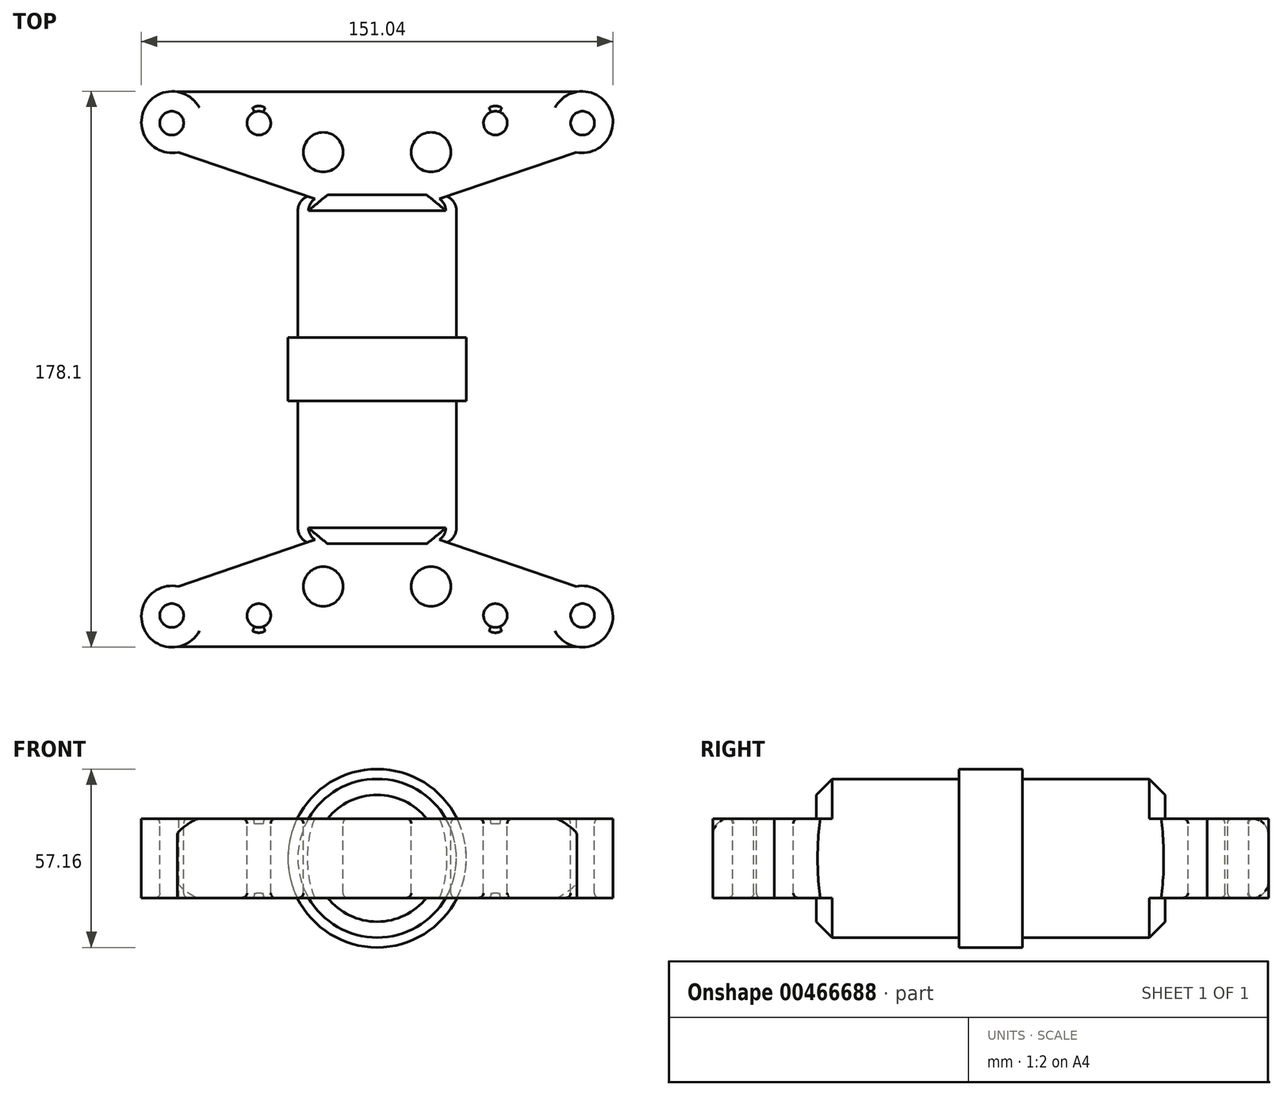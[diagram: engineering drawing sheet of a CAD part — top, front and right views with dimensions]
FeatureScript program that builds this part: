
annotation { "Feature Type Name" : "Feature", "Feature Type Description" : "" }
export const myFeature = defineFeature(function(context is Context, id is Id, definition is map)
    precondition{}
    {
        {
            var Q0;
            Q0=qCreatedBy(makeId("Top.planeOp"),FACE);
            var sketch = newSketch(context, id + "F0", { "sketchPlane" : qUnion([Q0])});
            skLineSegment(sketch, "E0.bottom", {"start": v(0, 0) * mm, "end": v(-76.2, 0) * mm, "construction": true});
            skLineSegment(sketch, "E0.left", {"start": v(0, 0) * mm, "end": v(0, 88.9) * mm, "construction": true});
            skLineSegment(sketch, "E0.right", {"start": v(-76.2, 0) * mm, "end": v(-76.2, 88.9) * mm, "construction": true});
            skLineSegment(sketch, "E1.MirrorCS", {"start": v(0, 88.9) * mm, "end": v(76.2, 88.9) * mm, "construction": true});
            skLineSegment(sketch, "E2.MirrorCS", {"start": v(76.2, 0) * mm, "end": v(76.2, 88.9) * mm, "construction": true});
            skLineSegment(sketch, "E3.MirrorCS", {"start": v(0, 0) * mm, "end": v(76.2, 0) * mm});
            skLineSegment(sketch, "E4.MirrorCS", {"start": v(0, 0) * mm, "end": v(0, -88.9) * mm, "construction": true});
            skLineSegment(sketch, "E5.MirrorCS", {"start": v(-76.2, 0) * mm, "end": v(-76.2, -88.9) * mm, "construction": true});
            skLineSegment(sketch, "E6.MirrorCS", {"start": v(0, 0) * mm, "end": v(76.2, 0) * mm, "construction": true});
            skLineSegment(sketch, "E7.MirrorCS", {"start": v(76.2, 0) * mm, "end": v(76.2, -88.9) * mm, "construction": true});
            skLineSegment(sketch, "E8.MirrorCS", {"start": v(0, -88.9) * mm, "end": v(76.2, -88.9) * mm, "construction": true});
            skArc(sketch, "E9", {"start": v(-63.96, 88.9) * mm, "mid": v(-75.52, 79.06) * mm, "end": v(-63.7, 69.55) * mm});
            skLineSegment(sketch, "E10", {"start": v(-63.96, 88.9) * mm, "end": v(0, 88.9) * mm});
            skLineSegment(sketch, "E11", {"start": v(-63.7, 69.55) * mm, "end": v(-20.52, 54.8) * mm});
            skLineSegment(sketch, "E12", {"start": v(-20.52, 54.8) * mm, "end": v(-20.52, 0) * mm});
            skLineSegment(sketch, "E13.MirrorCS", {"start": v(20.52, 54.8) * mm, "end": v(20.52, 0) * mm});
            skLineSegment(sketch, "E14.MirrorCS", {"start": v(63.7, 69.55) * mm, "end": v(20.52, 54.8) * mm});
            skLineSegment(sketch, "E15.MirrorCS", {"start": v(63.96, 88.9) * mm, "end": v(0, 88.9) * mm});
            skArc(sketch, "E16.MirrorCS", {"start": v(63.96, 88.9) * mm, "mid": v(75.52, 79.06) * mm, "end": v(63.7, 69.55) * mm});
            skLineSegment(sketch, "E17.MirrorCS", {"start": v(-63.96, -88.9) * mm, "end": v(0, -88.9) * mm});
            skArc(sketch, "E18.MirrorCS", {"start": v(-63.96, -88.9) * mm, "mid": v(-75.52, -79.06) * mm, "end": v(-63.7, -69.55) * mm});
            skLineSegment(sketch, "E19.MirrorCS", {"start": v(-20.52, -54.8) * mm, "end": v(-20.52, 0) * mm});
            skLineSegment(sketch, "E20.MirrorCS", {"start": v(-63.7, -69.55) * mm, "end": v(-20.52, -54.8) * mm});
            skLineSegment(sketch, "E21.MirrorCS", {"start": v(20.52, -54.8) * mm, "end": v(20.52, 0) * mm});
            skLineSegment(sketch, "E22.MirrorCS", {"start": v(63.7, -69.55) * mm, "end": v(20.52, -54.8) * mm});
            skArc(sketch, "E23.MirrorCS", {"start": v(63.96, -88.9) * mm, "mid": v(75.52, -79.06) * mm, "end": v(63.7, -69.55) * mm});
            skLineSegment(sketch, "E24.MirrorCS", {"start": v(63.96, -88.9) * mm, "end": v(0, -88.9) * mm});
            skSolve(sketch);
        }
        {
            var Q0;
            Q0=qCreatedBy(makeId("Front.planeOp"),FACE);
            var sketch = newSketch(context, id + "F1", { "sketchPlane" : qUnion([Q0])});
            skCircle(sketch, "E25", {"center": v(0, 0) * mm, "radius": 25.4 * mm});
            skSolve(sketch);
        }
        {
            var Q0;
            Q0 = qSketchRegion(id + "F0", true);
            extrude(context, id + "F2", {"entities" : qUnion([Q0]), "depth" : 12.7 * mm, "hasSecondDirection" : true, "secondDirectionOppositeDirection" : true, "secondDirectionDepth" : 12.7 * mm});
        }
        {
            var Q0;
            Q0 = qSketchRegion(id + "F1", true);
            extrude(context, id + "F3", {"entities" : qUnion([Q0]), "operationType" : NewBodyOperationType.ADD, "depth" : 55.88 * mm, "hasSecondDirection" : true, "secondDirectionOppositeDirection" : true, "secondDirectionDepth" : 55.88 * mm});
        }
        {
            var Q0;
            {var subQ0=sQuery(id+"F1.wireOp",EDGE,"E25");Q0=makeQuery(id+"F3.boolean.opBoolean","SPLIT",EDGE,{"disambiguationData":[TD([makeQuery(id+"F2.opExtrude","CAP_FACE",FACE,{"disambiguationData":[OSD([sQuery(id+"F0.wireOp",EDGE,"E9"),sQuery(id+"F0.wireOp",EDGE,"E10"),sQuery(id+"F0.wireOp",EDGE,"E11"),sQuery(id+"F0.wireOp",EDGE,"E12"),sQuery(id+"F0.wireOp",EDGE,"E14.MirrorCS"),sQuery(id+"F0.wireOp",EDGE,"E15.MirrorCS"),sQuery(id+"F0.wireOp",EDGE,"E16.MirrorCS"),sQuery(id+"F0.wireOp",EDGE,"E13.MirrorCS"),sQuery(id+"F0.wireOp",EDGE,"E17.MirrorCS"),sQuery(id+"F0.wireOp",EDGE,"E18.MirrorCS"),sQuery(id+"F0.wireOp",EDGE,"E19.MirrorCS"),sQuery(id+"F0.wireOp",EDGE,"E20.MirrorCS"),sQuery(id+"F0.wireOp",EDGE,"E21.MirrorCS"),sQuery(id+"F0.wireOp",EDGE,"E22.MirrorCS"),sQuery(id+"F0.wireOp",EDGE,"E23.MirrorCS"),sQuery(id+"F0.wireOp",EDGE,"E24.MirrorCS")])],"isStart":false})])],"derivedFrom":makeQuery(id+"F3.opExtrude","CAP_EDGE",EDGE,{"disambiguationData":[OSD([subQ0])],"isStart":true})});}
            var Q1;
            {var subQ0=sQuery(id+"F1.wireOp",EDGE,"E25");Q1=makeQuery(id+"F3.boolean.opBoolean","SPLIT",EDGE,{"disambiguationData":[TD([makeQuery(id+"F2.opExtrude","CAP_FACE",FACE,{"disambiguationData":[OSD([sQuery(id+"F0.wireOp",EDGE,"E9"),sQuery(id+"F0.wireOp",EDGE,"E10"),sQuery(id+"F0.wireOp",EDGE,"E11"),sQuery(id+"F0.wireOp",EDGE,"E12"),sQuery(id+"F0.wireOp",EDGE,"E14.MirrorCS"),sQuery(id+"F0.wireOp",EDGE,"E15.MirrorCS"),sQuery(id+"F0.wireOp",EDGE,"E16.MirrorCS"),sQuery(id+"F0.wireOp",EDGE,"E13.MirrorCS"),sQuery(id+"F0.wireOp",EDGE,"E17.MirrorCS"),sQuery(id+"F0.wireOp",EDGE,"E18.MirrorCS"),sQuery(id+"F0.wireOp",EDGE,"E19.MirrorCS"),sQuery(id+"F0.wireOp",EDGE,"E20.MirrorCS"),sQuery(id+"F0.wireOp",EDGE,"E21.MirrorCS"),sQuery(id+"F0.wireOp",EDGE,"E22.MirrorCS"),sQuery(id+"F0.wireOp",EDGE,"E23.MirrorCS"),sQuery(id+"F0.wireOp",EDGE,"E24.MirrorCS")])],"isStart":true})])],"derivedFrom":makeQuery(id+"F3.opExtrude","CAP_EDGE",EDGE,{"disambiguationData":[OSD([subQ0])],"isStart":true})});}
            var Q2;
            {var subQ0=sQuery(id+"F1.wireOp",EDGE,"E25");Q2=makeQuery(id+"F3.boolean.opBoolean","SPLIT",EDGE,{"disambiguationData":[TD([makeQuery(id+"F2.opExtrude","CAP_FACE",FACE,{"disambiguationData":[OSD([sQuery(id+"F0.wireOp",EDGE,"E9"),sQuery(id+"F0.wireOp",EDGE,"E10"),sQuery(id+"F0.wireOp",EDGE,"E11"),sQuery(id+"F0.wireOp",EDGE,"E12"),sQuery(id+"F0.wireOp",EDGE,"E14.MirrorCS"),sQuery(id+"F0.wireOp",EDGE,"E15.MirrorCS"),sQuery(id+"F0.wireOp",EDGE,"E16.MirrorCS"),sQuery(id+"F0.wireOp",EDGE,"E13.MirrorCS"),sQuery(id+"F0.wireOp",EDGE,"E17.MirrorCS"),sQuery(id+"F0.wireOp",EDGE,"E18.MirrorCS"),sQuery(id+"F0.wireOp",EDGE,"E19.MirrorCS"),sQuery(id+"F0.wireOp",EDGE,"E20.MirrorCS"),sQuery(id+"F0.wireOp",EDGE,"E21.MirrorCS"),sQuery(id+"F0.wireOp",EDGE,"E22.MirrorCS"),sQuery(id+"F0.wireOp",EDGE,"E23.MirrorCS"),sQuery(id+"F0.wireOp",EDGE,"E24.MirrorCS")])],"isStart":true})])],"derivedFrom":makeQuery(id+"F3.opExtrude","CAP_EDGE",EDGE,{"disambiguationData":[OSD([subQ0])],"isStart":false})});}
            var Q3;
            {var subQ0=sQuery(id+"F1.wireOp",EDGE,"E25");Q3=makeQuery(id+"F3.boolean.opBoolean","SPLIT",EDGE,{"disambiguationData":[TD([makeQuery(id+"F2.opExtrude","CAP_FACE",FACE,{"disambiguationData":[OSD([sQuery(id+"F0.wireOp",EDGE,"E9"),sQuery(id+"F0.wireOp",EDGE,"E10"),sQuery(id+"F0.wireOp",EDGE,"E11"),sQuery(id+"F0.wireOp",EDGE,"E12"),sQuery(id+"F0.wireOp",EDGE,"E14.MirrorCS"),sQuery(id+"F0.wireOp",EDGE,"E15.MirrorCS"),sQuery(id+"F0.wireOp",EDGE,"E16.MirrorCS"),sQuery(id+"F0.wireOp",EDGE,"E13.MirrorCS"),sQuery(id+"F0.wireOp",EDGE,"E17.MirrorCS"),sQuery(id+"F0.wireOp",EDGE,"E18.MirrorCS"),sQuery(id+"F0.wireOp",EDGE,"E19.MirrorCS"),sQuery(id+"F0.wireOp",EDGE,"E20.MirrorCS"),sQuery(id+"F0.wireOp",EDGE,"E21.MirrorCS"),sQuery(id+"F0.wireOp",EDGE,"E22.MirrorCS"),sQuery(id+"F0.wireOp",EDGE,"E23.MirrorCS"),sQuery(id+"F0.wireOp",EDGE,"E24.MirrorCS")])],"isStart":false})])],"derivedFrom":makeQuery(id+"F3.opExtrude","CAP_EDGE",EDGE,{"disambiguationData":[OSD([subQ0])],"isStart":false})});}
            chamfer(context, id + "F4", {"entities" : qUnion([Q0, Q1, Q2, Q3]), "width" : 5.08 * mm, "tangentPropagation" : true});
        }
        {
            var Q0;
            {var subQ0=sQuery(id+"F1.wireOp",EDGE,"E25");Q0=makeQuery(id+"F3.boolean.opBoolean","SPLIT",EDGE,{"disambiguationData":[TD([makeQuery(id+"F2.opExtrude","SWEPT_FACE",FACE,{"disambiguationData":[OSD([sQuery(id+"F0.wireOp",EDGE,"E14.MirrorCS")])]})])],"derivedFrom":makeQuery(id+"F3.opExtrude","CAP_EDGE",EDGE,{"disambiguationData":[OSD([subQ0])],"isStart":true})});}
            var Q1;
            {var subQ0=sQuery(id+"F1.wireOp",EDGE,"E25");Q1=makeQuery(id+"F3.boolean.opBoolean","SPLIT",EDGE,{"disambiguationData":[TD([makeQuery(id+"F2.opExtrude","SWEPT_FACE",FACE,{"disambiguationData":[OSD([sQuery(id+"F0.wireOp",EDGE,"E11")])]})])],"derivedFrom":makeQuery(id+"F3.opExtrude","CAP_EDGE",EDGE,{"disambiguationData":[OSD([subQ0])],"isStart":true})});}
            var Q2;
            {var subQ0=sQuery(id+"F1.wireOp",EDGE,"E25");Q2=makeQuery(id+"F3.boolean.opBoolean","SPLIT",EDGE,{"disambiguationData":[TD([makeQuery(id+"F2.opExtrude","SWEPT_FACE",FACE,{"disambiguationData":[OSD([sQuery(id+"F0.wireOp",EDGE,"E20.MirrorCS")])]})])],"derivedFrom":makeQuery(id+"F3.opExtrude","CAP_EDGE",EDGE,{"disambiguationData":[OSD([subQ0])],"isStart":false})});}
            var Q3;
            {var subQ0=sQuery(id+"F1.wireOp",EDGE,"E25");Q3=makeQuery(id+"F3.boolean.opBoolean","SPLIT",EDGE,{"disambiguationData":[TD([makeQuery(id+"F2.opExtrude","SWEPT_FACE",FACE,{"disambiguationData":[OSD([sQuery(id+"F0.wireOp",EDGE,"E22.MirrorCS")])]})])],"derivedFrom":makeQuery(id+"F3.opExtrude","CAP_EDGE",EDGE,{"disambiguationData":[OSD([subQ0])],"isStart":false})});}
            fillet(context, id + "F5", {"entities" : qUnion([Q0, Q1, Q2, Q3]), "radius" : 5.08 * mm, "tangentPropagation" : true, "allowEdgeOverflow" : false});
        }
        {
            var Q0;
            Q0=makeQuery(id+"F2.opExtrude","CAP_EDGE",EDGE,{"disambiguationData":[OSD([sQuery(id+"F0.wireOp",EDGE,"E17.MirrorCS"),sQuery(id+"F0.wireOp",EDGE,"E24.MirrorCS")])],"isStart":false});
            var Q1;
            Q1=makeQuery(id+"F2.opExtrude","CAP_EDGE",EDGE,{"disambiguationData":[OSD([sQuery(id+"F0.wireOp",EDGE,"E10"),sQuery(id+"F0.wireOp",EDGE,"E15.MirrorCS")])],"isStart":false});
            var Q2;
            Q2=makeQuery(id+"F2.opExtrude","CAP_EDGE",EDGE,{"disambiguationData":[OSD([sQuery(id+"F0.wireOp",EDGE,"E10"),sQuery(id+"F0.wireOp",EDGE,"E15.MirrorCS")])],"isStart":true});
            fillet(context, id + "F6", {"entities" : qUnion([Q0, Q1, Q2]), "radius" : 5.08 * mm, "tangentPropagation" : true, "allowEdgeOverflow" : false});
        }
        {
            var Q0;
            Q0=qCreatedBy(makeId("Top.planeOp"),FACE);
            var sketch = newSketch(context, id + "F7", { "sketchPlane" : qUnion([Q0])});
            skLineSegment(sketch, "E26", {"start": v(-65.8, 78.88) * mm, "end": v(0, 78.88) * mm, "construction": true});
            skCircle(sketch, "E27", {"center": v(-65.8, 78.88) * mm, "radius": 3.81 * mm});
            skCircle(sketch, "E28", {"center": v(-37.89, 78.88) * mm, "radius": 3.81 * mm});
            skLineSegment(sketch, "E29", {"start": v(-17.28, 78.88) * mm, "end": v(-17.28, 69.57) * mm, "construction": true});
            skLineSegment(sketch, "E30", {"start": v(-17.28, 69.57) * mm, "end": v(0, 69.57) * mm, "construction": true});
            skCircle(sketch, "E31", {"center": v(-17.28, 69.57) * mm, "radius": 6.35 * mm});
            skCircle(sketch, "E32.MirrorC", {"center": v(17.28, 69.57) * mm, "radius": 6.35 * mm});
            skCircle(sketch, "E33.MirrorC", {"center": v(37.89, 78.88) * mm, "radius": 3.81 * mm});
            skCircle(sketch, "E34.MirrorC", {"center": v(65.8, 78.88) * mm, "radius": 3.81 * mm});
            skCircle(sketch, "E35.MirrorC", {"center": v(65.8, -78.88) * mm, "radius": 3.81 * mm});
            skCircle(sketch, "E36.MirrorC", {"center": v(37.89, -78.88) * mm, "radius": 3.81 * mm});
            skCircle(sketch, "E37.MirrorC", {"center": v(17.28, -69.57) * mm, "radius": 6.35 * mm});
            skCircle(sketch, "E38.MirrorC", {"center": v(-17.28, -69.57) * mm, "radius": 6.35 * mm});
            skCircle(sketch, "E39.MirrorC", {"center": v(-37.89, -78.88) * mm, "radius": 3.81 * mm});
            skCircle(sketch, "E40.MirrorC", {"center": v(-65.8, -78.88) * mm, "radius": 3.81 * mm});
            skSolve(sketch);
        }
        {
            var Q0;
            Q0 = qSketchRegion(id + "F7", true);
            extrude(context, id + "F8", {"entities" : qUnion([Q0]), "operationType" : NewBodyOperationType.REMOVE, "oppositeDirection" : true, "depth" : 25.4 * mm, "hasSecondDirection" : true, "secondDirectionOppositeDirection" : false, "secondDirectionDepth" : 25.4 * mm});
        }
        {
            var Q0;
            {var subQ0=sQuery(id+"F0.wireOp",EDGE,"E14.MirrorCS");var subQ1=sQuery(id+"F0.wireOp",EDGE,"E11");var subQ3=sQuery(id+"F0.wireOp",EDGE,"E15.MirrorCS");var subQ4=sQuery(id+"F0.wireOp",EDGE,"E10");var subQ5=sQuery(id+"F0.wireOp",EDGE,"E9");var subQ6=sQuery(id+"F0.wireOp",EDGE,"E16.MirrorCS");Q0=makeQuery(id+"F8.boolean.opBoolean","INTERSECT",EDGE,{"derivedFrom":[makeQuery(id+"F3.boolean.opBoolean","SPLIT",FACE,{"disambiguationData":[TD([makeQuery(id+"F2.opExtrude","SWEPT_FACE",FACE,{"disambiguationData":[OSD([subQ5])]})])],"derivedFrom":makeQuery(id+"F2.opExtrude","CAP_FACE",FACE,{"disambiguationData":[OSD([subQ5,subQ4,subQ1,sQuery(id+"F0.wireOp",EDGE,"E12"),subQ0,subQ3,subQ6,sQuery(id+"F0.wireOp",EDGE,"E13.MirrorCS"),sQuery(id+"F0.wireOp",EDGE,"E17.MirrorCS"),sQuery(id+"F0.wireOp",EDGE,"E18.MirrorCS"),sQuery(id+"F0.wireOp",EDGE,"E19.MirrorCS"),sQuery(id+"F0.wireOp",EDGE,"E20.MirrorCS"),sQuery(id+"F0.wireOp",EDGE,"E21.MirrorCS"),sQuery(id+"F0.wireOp",EDGE,"E22.MirrorCS"),sQuery(id+"F0.wireOp",EDGE,"E23.MirrorCS"),sQuery(id+"F0.wireOp",EDGE,"E24.MirrorCS")])],"isStart":false})}),makeQuery(id+"F8.opExtrude","SWEPT_FACE",FACE,{"disambiguationData":[OSD([sQuery(id+"F7.wireOp",EDGE,"E27")])]})]});}
            var Q1;
            {var subQ0=sQuery(id+"F0.wireOp",EDGE,"E14.MirrorCS");var subQ1=sQuery(id+"F0.wireOp",EDGE,"E11");var subQ3=sQuery(id+"F0.wireOp",EDGE,"E15.MirrorCS");var subQ4=sQuery(id+"F0.wireOp",EDGE,"E10");var subQ5=sQuery(id+"F0.wireOp",EDGE,"E9");var subQ6=sQuery(id+"F0.wireOp",EDGE,"E16.MirrorCS");Q1=makeQuery(id+"F8.boolean.opBoolean","INTERSECT",EDGE,{"derivedFrom":[makeQuery(id+"F3.boolean.opBoolean","SPLIT",FACE,{"disambiguationData":[TD([makeQuery(id+"F2.opExtrude","SWEPT_FACE",FACE,{"disambiguationData":[OSD([subQ5])]})])],"derivedFrom":makeQuery(id+"F2.opExtrude","CAP_FACE",FACE,{"disambiguationData":[OSD([subQ5,subQ4,subQ1,sQuery(id+"F0.wireOp",EDGE,"E12"),subQ0,subQ3,subQ6,sQuery(id+"F0.wireOp",EDGE,"E13.MirrorCS"),sQuery(id+"F0.wireOp",EDGE,"E17.MirrorCS"),sQuery(id+"F0.wireOp",EDGE,"E18.MirrorCS"),sQuery(id+"F0.wireOp",EDGE,"E19.MirrorCS"),sQuery(id+"F0.wireOp",EDGE,"E20.MirrorCS"),sQuery(id+"F0.wireOp",EDGE,"E21.MirrorCS"),sQuery(id+"F0.wireOp",EDGE,"E22.MirrorCS"),sQuery(id+"F0.wireOp",EDGE,"E23.MirrorCS"),sQuery(id+"F0.wireOp",EDGE,"E24.MirrorCS")])],"isStart":false})}),makeQuery(id+"F8.opExtrude","SWEPT_FACE",FACE,{"disambiguationData":[OSD([sQuery(id+"F7.wireOp",EDGE,"E28")])]})]});}
            var Q2;
            {var subQ0=sQuery(id+"F0.wireOp",EDGE,"E14.MirrorCS");var subQ1=sQuery(id+"F0.wireOp",EDGE,"E11");var subQ3=sQuery(id+"F0.wireOp",EDGE,"E15.MirrorCS");var subQ4=sQuery(id+"F0.wireOp",EDGE,"E10");var subQ5=sQuery(id+"F0.wireOp",EDGE,"E9");var subQ6=sQuery(id+"F0.wireOp",EDGE,"E16.MirrorCS");Q2=makeQuery(id+"F8.boolean.opBoolean","INTERSECT",EDGE,{"derivedFrom":[makeQuery(id+"F3.boolean.opBoolean","SPLIT",FACE,{"disambiguationData":[TD([makeQuery(id+"F2.opExtrude","SWEPT_FACE",FACE,{"disambiguationData":[OSD([subQ5])]})])],"derivedFrom":makeQuery(id+"F2.opExtrude","CAP_FACE",FACE,{"disambiguationData":[OSD([subQ5,subQ4,subQ1,sQuery(id+"F0.wireOp",EDGE,"E12"),subQ0,subQ3,subQ6,sQuery(id+"F0.wireOp",EDGE,"E13.MirrorCS"),sQuery(id+"F0.wireOp",EDGE,"E17.MirrorCS"),sQuery(id+"F0.wireOp",EDGE,"E18.MirrorCS"),sQuery(id+"F0.wireOp",EDGE,"E19.MirrorCS"),sQuery(id+"F0.wireOp",EDGE,"E20.MirrorCS"),sQuery(id+"F0.wireOp",EDGE,"E21.MirrorCS"),sQuery(id+"F0.wireOp",EDGE,"E22.MirrorCS"),sQuery(id+"F0.wireOp",EDGE,"E23.MirrorCS"),sQuery(id+"F0.wireOp",EDGE,"E24.MirrorCS")])],"isStart":false})}),makeQuery(id+"F8.opExtrude","SWEPT_FACE",FACE,{"disambiguationData":[OSD([sQuery(id+"F7.wireOp",EDGE,"E31")])]})]});}
            var Q3;
            {var subQ0=sQuery(id+"F0.wireOp",EDGE,"E14.MirrorCS");var subQ1=sQuery(id+"F0.wireOp",EDGE,"E11");var subQ3=sQuery(id+"F0.wireOp",EDGE,"E15.MirrorCS");var subQ4=sQuery(id+"F0.wireOp",EDGE,"E10");var subQ5=sQuery(id+"F0.wireOp",EDGE,"E9");var subQ6=sQuery(id+"F0.wireOp",EDGE,"E16.MirrorCS");Q3=makeQuery(id+"F8.boolean.opBoolean","INTERSECT",EDGE,{"derivedFrom":[makeQuery(id+"F3.boolean.opBoolean","SPLIT",FACE,{"disambiguationData":[TD([makeQuery(id+"F2.opExtrude","SWEPT_FACE",FACE,{"disambiguationData":[OSD([subQ5])]})])],"derivedFrom":makeQuery(id+"F2.opExtrude","CAP_FACE",FACE,{"disambiguationData":[OSD([subQ5,subQ4,subQ1,sQuery(id+"F0.wireOp",EDGE,"E12"),subQ0,subQ3,subQ6,sQuery(id+"F0.wireOp",EDGE,"E13.MirrorCS"),sQuery(id+"F0.wireOp",EDGE,"E17.MirrorCS"),sQuery(id+"F0.wireOp",EDGE,"E18.MirrorCS"),sQuery(id+"F0.wireOp",EDGE,"E19.MirrorCS"),sQuery(id+"F0.wireOp",EDGE,"E20.MirrorCS"),sQuery(id+"F0.wireOp",EDGE,"E21.MirrorCS"),sQuery(id+"F0.wireOp",EDGE,"E22.MirrorCS"),sQuery(id+"F0.wireOp",EDGE,"E23.MirrorCS"),sQuery(id+"F0.wireOp",EDGE,"E24.MirrorCS")])],"isStart":false})}),makeQuery(id+"F8.opExtrude","SWEPT_FACE",FACE,{"disambiguationData":[OSD([sQuery(id+"F7.wireOp",EDGE,"E32.MirrorC")])]})]});}
            var Q4;
            {var subQ0=sQuery(id+"F0.wireOp",EDGE,"E14.MirrorCS");var subQ1=sQuery(id+"F0.wireOp",EDGE,"E11");var subQ3=sQuery(id+"F0.wireOp",EDGE,"E15.MirrorCS");var subQ4=sQuery(id+"F0.wireOp",EDGE,"E10");var subQ5=sQuery(id+"F0.wireOp",EDGE,"E9");var subQ6=sQuery(id+"F0.wireOp",EDGE,"E16.MirrorCS");Q4=makeQuery(id+"F8.boolean.opBoolean","INTERSECT",EDGE,{"derivedFrom":[makeQuery(id+"F3.boolean.opBoolean","SPLIT",FACE,{"disambiguationData":[TD([makeQuery(id+"F2.opExtrude","SWEPT_FACE",FACE,{"disambiguationData":[OSD([subQ5])]})])],"derivedFrom":makeQuery(id+"F2.opExtrude","CAP_FACE",FACE,{"disambiguationData":[OSD([subQ5,subQ4,subQ1,sQuery(id+"F0.wireOp",EDGE,"E12"),subQ0,subQ3,subQ6,sQuery(id+"F0.wireOp",EDGE,"E13.MirrorCS"),sQuery(id+"F0.wireOp",EDGE,"E17.MirrorCS"),sQuery(id+"F0.wireOp",EDGE,"E18.MirrorCS"),sQuery(id+"F0.wireOp",EDGE,"E19.MirrorCS"),sQuery(id+"F0.wireOp",EDGE,"E20.MirrorCS"),sQuery(id+"F0.wireOp",EDGE,"E21.MirrorCS"),sQuery(id+"F0.wireOp",EDGE,"E22.MirrorCS"),sQuery(id+"F0.wireOp",EDGE,"E23.MirrorCS"),sQuery(id+"F0.wireOp",EDGE,"E24.MirrorCS")])],"isStart":false})}),makeQuery(id+"F8.opExtrude","SWEPT_FACE",FACE,{"disambiguationData":[OSD([sQuery(id+"F7.wireOp",EDGE,"E33.MirrorC")])]})]});}
            var Q5;
            {var subQ0=sQuery(id+"F0.wireOp",EDGE,"E14.MirrorCS");var subQ1=sQuery(id+"F0.wireOp",EDGE,"E11");var subQ3=sQuery(id+"F0.wireOp",EDGE,"E15.MirrorCS");var subQ4=sQuery(id+"F0.wireOp",EDGE,"E10");var subQ5=sQuery(id+"F0.wireOp",EDGE,"E9");var subQ6=sQuery(id+"F0.wireOp",EDGE,"E16.MirrorCS");Q5=makeQuery(id+"F8.boolean.opBoolean","INTERSECT",EDGE,{"derivedFrom":[makeQuery(id+"F3.boolean.opBoolean","SPLIT",FACE,{"disambiguationData":[TD([makeQuery(id+"F2.opExtrude","SWEPT_FACE",FACE,{"disambiguationData":[OSD([subQ5])]})])],"derivedFrom":makeQuery(id+"F2.opExtrude","CAP_FACE",FACE,{"disambiguationData":[OSD([subQ5,subQ4,subQ1,sQuery(id+"F0.wireOp",EDGE,"E12"),subQ0,subQ3,subQ6,sQuery(id+"F0.wireOp",EDGE,"E13.MirrorCS"),sQuery(id+"F0.wireOp",EDGE,"E17.MirrorCS"),sQuery(id+"F0.wireOp",EDGE,"E18.MirrorCS"),sQuery(id+"F0.wireOp",EDGE,"E19.MirrorCS"),sQuery(id+"F0.wireOp",EDGE,"E20.MirrorCS"),sQuery(id+"F0.wireOp",EDGE,"E21.MirrorCS"),sQuery(id+"F0.wireOp",EDGE,"E22.MirrorCS"),sQuery(id+"F0.wireOp",EDGE,"E23.MirrorCS"),sQuery(id+"F0.wireOp",EDGE,"E24.MirrorCS")])],"isStart":false})}),makeQuery(id+"F8.opExtrude","SWEPT_FACE",FACE,{"disambiguationData":[OSD([sQuery(id+"F7.wireOp",EDGE,"E34.MirrorC")])]})]});}
            var Q6;
            {var subQ0=sQuery(id+"F0.wireOp",EDGE,"E22.MirrorCS");var subQ1=sQuery(id+"F0.wireOp",EDGE,"E20.MirrorCS");var subQ2=sQuery(id+"F0.wireOp",EDGE,"E18.MirrorCS");var subQ3=sQuery(id+"F0.wireOp",EDGE,"E24.MirrorCS");var subQ4=sQuery(id+"F0.wireOp",EDGE,"E17.MirrorCS");var subQ5=sQuery(id+"F0.wireOp",EDGE,"E23.MirrorCS");Q6=makeQuery(id+"F8.boolean.opBoolean","INTERSECT",EDGE,{"derivedFrom":[makeQuery(id+"F3.boolean.opBoolean","SPLIT",FACE,{"disambiguationData":[TD([makeQuery(id+"F2.opExtrude","SWEPT_FACE",FACE,{"disambiguationData":[OSD([subQ2])]})])],"derivedFrom":makeQuery(id+"F2.opExtrude","CAP_FACE",FACE,{"disambiguationData":[OSD([sQuery(id+"F0.wireOp",EDGE,"E9"),sQuery(id+"F0.wireOp",EDGE,"E10"),sQuery(id+"F0.wireOp",EDGE,"E11"),sQuery(id+"F0.wireOp",EDGE,"E12"),sQuery(id+"F0.wireOp",EDGE,"E14.MirrorCS"),sQuery(id+"F0.wireOp",EDGE,"E15.MirrorCS"),sQuery(id+"F0.wireOp",EDGE,"E16.MirrorCS"),sQuery(id+"F0.wireOp",EDGE,"E13.MirrorCS"),subQ4,subQ2,sQuery(id+"F0.wireOp",EDGE,"E19.MirrorCS"),subQ1,sQuery(id+"F0.wireOp",EDGE,"E21.MirrorCS"),subQ0,subQ5,subQ3])],"isStart":false})}),makeQuery(id+"F8.opExtrude","SWEPT_FACE",FACE,{"disambiguationData":[OSD([sQuery(id+"F7.wireOp",EDGE,"E38.MirrorC")])]})]});}
            var Q7;
            {var subQ0=sQuery(id+"F0.wireOp",EDGE,"E22.MirrorCS");var subQ1=sQuery(id+"F0.wireOp",EDGE,"E20.MirrorCS");var subQ2=sQuery(id+"F0.wireOp",EDGE,"E18.MirrorCS");var subQ3=sQuery(id+"F0.wireOp",EDGE,"E24.MirrorCS");var subQ4=sQuery(id+"F0.wireOp",EDGE,"E17.MirrorCS");var subQ5=sQuery(id+"F0.wireOp",EDGE,"E23.MirrorCS");Q7=makeQuery(id+"F8.boolean.opBoolean","INTERSECT",EDGE,{"derivedFrom":[makeQuery(id+"F3.boolean.opBoolean","SPLIT",FACE,{"disambiguationData":[TD([makeQuery(id+"F2.opExtrude","SWEPT_FACE",FACE,{"disambiguationData":[OSD([subQ2])]})])],"derivedFrom":makeQuery(id+"F2.opExtrude","CAP_FACE",FACE,{"disambiguationData":[OSD([sQuery(id+"F0.wireOp",EDGE,"E9"),sQuery(id+"F0.wireOp",EDGE,"E10"),sQuery(id+"F0.wireOp",EDGE,"E11"),sQuery(id+"F0.wireOp",EDGE,"E12"),sQuery(id+"F0.wireOp",EDGE,"E14.MirrorCS"),sQuery(id+"F0.wireOp",EDGE,"E15.MirrorCS"),sQuery(id+"F0.wireOp",EDGE,"E16.MirrorCS"),sQuery(id+"F0.wireOp",EDGE,"E13.MirrorCS"),subQ4,subQ2,sQuery(id+"F0.wireOp",EDGE,"E19.MirrorCS"),subQ1,sQuery(id+"F0.wireOp",EDGE,"E21.MirrorCS"),subQ0,subQ5,subQ3])],"isStart":false})}),makeQuery(id+"F8.opExtrude","SWEPT_FACE",FACE,{"disambiguationData":[OSD([sQuery(id+"F7.wireOp",EDGE,"E37.MirrorC")])]})]});}
            var Q8;
            {var subQ0=sQuery(id+"F0.wireOp",EDGE,"E22.MirrorCS");var subQ1=sQuery(id+"F0.wireOp",EDGE,"E20.MirrorCS");var subQ2=sQuery(id+"F0.wireOp",EDGE,"E18.MirrorCS");var subQ3=sQuery(id+"F0.wireOp",EDGE,"E24.MirrorCS");var subQ4=sQuery(id+"F0.wireOp",EDGE,"E17.MirrorCS");var subQ5=sQuery(id+"F0.wireOp",EDGE,"E23.MirrorCS");Q8=makeQuery(id+"F8.boolean.opBoolean","INTERSECT",EDGE,{"derivedFrom":[makeQuery(id+"F3.boolean.opBoolean","SPLIT",FACE,{"disambiguationData":[TD([makeQuery(id+"F2.opExtrude","SWEPT_FACE",FACE,{"disambiguationData":[OSD([subQ2])]})])],"derivedFrom":makeQuery(id+"F2.opExtrude","CAP_FACE",FACE,{"disambiguationData":[OSD([sQuery(id+"F0.wireOp",EDGE,"E9"),sQuery(id+"F0.wireOp",EDGE,"E10"),sQuery(id+"F0.wireOp",EDGE,"E11"),sQuery(id+"F0.wireOp",EDGE,"E12"),sQuery(id+"F0.wireOp",EDGE,"E14.MirrorCS"),sQuery(id+"F0.wireOp",EDGE,"E15.MirrorCS"),sQuery(id+"F0.wireOp",EDGE,"E16.MirrorCS"),sQuery(id+"F0.wireOp",EDGE,"E13.MirrorCS"),subQ4,subQ2,sQuery(id+"F0.wireOp",EDGE,"E19.MirrorCS"),subQ1,sQuery(id+"F0.wireOp",EDGE,"E21.MirrorCS"),subQ0,subQ5,subQ3])],"isStart":false})}),makeQuery(id+"F8.opExtrude","SWEPT_FACE",FACE,{"disambiguationData":[OSD([sQuery(id+"F7.wireOp",EDGE,"E36.MirrorC")])]})]});}
            var Q9;
            {var subQ0=sQuery(id+"F0.wireOp",EDGE,"E22.MirrorCS");var subQ1=sQuery(id+"F0.wireOp",EDGE,"E20.MirrorCS");var subQ2=sQuery(id+"F0.wireOp",EDGE,"E18.MirrorCS");var subQ3=sQuery(id+"F0.wireOp",EDGE,"E24.MirrorCS");var subQ4=sQuery(id+"F0.wireOp",EDGE,"E17.MirrorCS");var subQ5=sQuery(id+"F0.wireOp",EDGE,"E23.MirrorCS");Q9=makeQuery(id+"F8.boolean.opBoolean","INTERSECT",EDGE,{"derivedFrom":[makeQuery(id+"F3.boolean.opBoolean","SPLIT",FACE,{"disambiguationData":[TD([makeQuery(id+"F2.opExtrude","SWEPT_FACE",FACE,{"disambiguationData":[OSD([subQ2])]})])],"derivedFrom":makeQuery(id+"F2.opExtrude","CAP_FACE",FACE,{"disambiguationData":[OSD([sQuery(id+"F0.wireOp",EDGE,"E9"),sQuery(id+"F0.wireOp",EDGE,"E10"),sQuery(id+"F0.wireOp",EDGE,"E11"),sQuery(id+"F0.wireOp",EDGE,"E12"),sQuery(id+"F0.wireOp",EDGE,"E14.MirrorCS"),sQuery(id+"F0.wireOp",EDGE,"E15.MirrorCS"),sQuery(id+"F0.wireOp",EDGE,"E16.MirrorCS"),sQuery(id+"F0.wireOp",EDGE,"E13.MirrorCS"),subQ4,subQ2,sQuery(id+"F0.wireOp",EDGE,"E19.MirrorCS"),subQ1,sQuery(id+"F0.wireOp",EDGE,"E21.MirrorCS"),subQ0,subQ5,subQ3])],"isStart":false})}),makeQuery(id+"F8.opExtrude","SWEPT_FACE",FACE,{"disambiguationData":[OSD([sQuery(id+"F7.wireOp",EDGE,"E35.MirrorC")])]})]});}
            var Q10;
            {var subQ0=sQuery(id+"F0.wireOp",EDGE,"E22.MirrorCS");var subQ1=sQuery(id+"F0.wireOp",EDGE,"E20.MirrorCS");var subQ2=sQuery(id+"F0.wireOp",EDGE,"E18.MirrorCS");var subQ3=sQuery(id+"F0.wireOp",EDGE,"E24.MirrorCS");var subQ4=sQuery(id+"F0.wireOp",EDGE,"E17.MirrorCS");var subQ5=sQuery(id+"F0.wireOp",EDGE,"E23.MirrorCS");Q10=makeQuery(id+"F8.boolean.opBoolean","INTERSECT",EDGE,{"derivedFrom":[makeQuery(id+"F3.boolean.opBoolean","SPLIT",FACE,{"disambiguationData":[TD([makeQuery(id+"F2.opExtrude","SWEPT_FACE",FACE,{"disambiguationData":[OSD([subQ2])]})])],"derivedFrom":makeQuery(id+"F2.opExtrude","CAP_FACE",FACE,{"disambiguationData":[OSD([sQuery(id+"F0.wireOp",EDGE,"E9"),sQuery(id+"F0.wireOp",EDGE,"E10"),sQuery(id+"F0.wireOp",EDGE,"E11"),sQuery(id+"F0.wireOp",EDGE,"E12"),sQuery(id+"F0.wireOp",EDGE,"E14.MirrorCS"),sQuery(id+"F0.wireOp",EDGE,"E15.MirrorCS"),sQuery(id+"F0.wireOp",EDGE,"E16.MirrorCS"),sQuery(id+"F0.wireOp",EDGE,"E13.MirrorCS"),subQ4,subQ2,sQuery(id+"F0.wireOp",EDGE,"E19.MirrorCS"),subQ1,sQuery(id+"F0.wireOp",EDGE,"E21.MirrorCS"),subQ0,subQ5,subQ3])],"isStart":false})}),makeQuery(id+"F8.opExtrude","SWEPT_FACE",FACE,{"disambiguationData":[OSD([sQuery(id+"F7.wireOp",EDGE,"E39.MirrorC")])]})]});}
            var Q11;
            {var subQ0=sQuery(id+"F0.wireOp",EDGE,"E22.MirrorCS");var subQ1=sQuery(id+"F0.wireOp",EDGE,"E20.MirrorCS");var subQ2=sQuery(id+"F0.wireOp",EDGE,"E18.MirrorCS");var subQ3=sQuery(id+"F0.wireOp",EDGE,"E24.MirrorCS");var subQ4=sQuery(id+"F0.wireOp",EDGE,"E17.MirrorCS");var subQ5=sQuery(id+"F0.wireOp",EDGE,"E23.MirrorCS");Q11=makeQuery(id+"F8.boolean.opBoolean","INTERSECT",EDGE,{"derivedFrom":[makeQuery(id+"F3.boolean.opBoolean","SPLIT",FACE,{"disambiguationData":[TD([makeQuery(id+"F2.opExtrude","SWEPT_FACE",FACE,{"disambiguationData":[OSD([subQ2])]})])],"derivedFrom":makeQuery(id+"F2.opExtrude","CAP_FACE",FACE,{"disambiguationData":[OSD([sQuery(id+"F0.wireOp",EDGE,"E9"),sQuery(id+"F0.wireOp",EDGE,"E10"),sQuery(id+"F0.wireOp",EDGE,"E11"),sQuery(id+"F0.wireOp",EDGE,"E12"),sQuery(id+"F0.wireOp",EDGE,"E14.MirrorCS"),sQuery(id+"F0.wireOp",EDGE,"E15.MirrorCS"),sQuery(id+"F0.wireOp",EDGE,"E16.MirrorCS"),sQuery(id+"F0.wireOp",EDGE,"E13.MirrorCS"),subQ4,subQ2,sQuery(id+"F0.wireOp",EDGE,"E19.MirrorCS"),subQ1,sQuery(id+"F0.wireOp",EDGE,"E21.MirrorCS"),subQ0,subQ5,subQ3])],"isStart":false})}),makeQuery(id+"F8.opExtrude","SWEPT_FACE",FACE,{"disambiguationData":[OSD([sQuery(id+"F7.wireOp",EDGE,"E40.MirrorC")])]})]});}
            var Q12;
            {var subQ0=sQuery(id+"F0.wireOp",EDGE,"E14.MirrorCS");var subQ1=sQuery(id+"F0.wireOp",EDGE,"E11");var subQ3=sQuery(id+"F0.wireOp",EDGE,"E15.MirrorCS");var subQ4=sQuery(id+"F0.wireOp",EDGE,"E10");var subQ5=sQuery(id+"F0.wireOp",EDGE,"E9");var subQ6=sQuery(id+"F0.wireOp",EDGE,"E16.MirrorCS");Q12=makeQuery(id+"F8.boolean.opBoolean","INTERSECT",EDGE,{"derivedFrom":[makeQuery(id+"F3.boolean.opBoolean","SPLIT",FACE,{"disambiguationData":[TD([makeQuery(id+"F2.opExtrude","SWEPT_FACE",FACE,{"disambiguationData":[OSD([subQ5])]})])],"derivedFrom":makeQuery(id+"F2.opExtrude","CAP_FACE",FACE,{"disambiguationData":[OSD([subQ5,subQ4,subQ1,sQuery(id+"F0.wireOp",EDGE,"E12"),subQ0,subQ3,subQ6,sQuery(id+"F0.wireOp",EDGE,"E13.MirrorCS"),sQuery(id+"F0.wireOp",EDGE,"E17.MirrorCS"),sQuery(id+"F0.wireOp",EDGE,"E18.MirrorCS"),sQuery(id+"F0.wireOp",EDGE,"E19.MirrorCS"),sQuery(id+"F0.wireOp",EDGE,"E20.MirrorCS"),sQuery(id+"F0.wireOp",EDGE,"E21.MirrorCS"),sQuery(id+"F0.wireOp",EDGE,"E22.MirrorCS"),sQuery(id+"F0.wireOp",EDGE,"E23.MirrorCS"),sQuery(id+"F0.wireOp",EDGE,"E24.MirrorCS")])],"isStart":true})}),makeQuery(id+"F8.opExtrude","SWEPT_FACE",FACE,{"disambiguationData":[OSD([sQuery(id+"F7.wireOp",EDGE,"E32.MirrorC")])]})]});}
            var Q13;
            {var subQ0=sQuery(id+"F0.wireOp",EDGE,"E14.MirrorCS");var subQ1=sQuery(id+"F0.wireOp",EDGE,"E11");var subQ3=sQuery(id+"F0.wireOp",EDGE,"E15.MirrorCS");var subQ4=sQuery(id+"F0.wireOp",EDGE,"E10");var subQ5=sQuery(id+"F0.wireOp",EDGE,"E9");var subQ6=sQuery(id+"F0.wireOp",EDGE,"E16.MirrorCS");Q13=makeQuery(id+"F8.boolean.opBoolean","INTERSECT",EDGE,{"derivedFrom":[makeQuery(id+"F3.boolean.opBoolean","SPLIT",FACE,{"disambiguationData":[TD([makeQuery(id+"F2.opExtrude","SWEPT_FACE",FACE,{"disambiguationData":[OSD([subQ5])]})])],"derivedFrom":makeQuery(id+"F2.opExtrude","CAP_FACE",FACE,{"disambiguationData":[OSD([subQ5,subQ4,subQ1,sQuery(id+"F0.wireOp",EDGE,"E12"),subQ0,subQ3,subQ6,sQuery(id+"F0.wireOp",EDGE,"E13.MirrorCS"),sQuery(id+"F0.wireOp",EDGE,"E17.MirrorCS"),sQuery(id+"F0.wireOp",EDGE,"E18.MirrorCS"),sQuery(id+"F0.wireOp",EDGE,"E19.MirrorCS"),sQuery(id+"F0.wireOp",EDGE,"E20.MirrorCS"),sQuery(id+"F0.wireOp",EDGE,"E21.MirrorCS"),sQuery(id+"F0.wireOp",EDGE,"E22.MirrorCS"),sQuery(id+"F0.wireOp",EDGE,"E23.MirrorCS"),sQuery(id+"F0.wireOp",EDGE,"E24.MirrorCS")])],"isStart":true})}),makeQuery(id+"F8.opExtrude","SWEPT_FACE",FACE,{"disambiguationData":[OSD([sQuery(id+"F7.wireOp",EDGE,"E33.MirrorC")])]})]});}
            var Q14;
            {var subQ0=sQuery(id+"F0.wireOp",EDGE,"E14.MirrorCS");var subQ1=sQuery(id+"F0.wireOp",EDGE,"E11");var subQ3=sQuery(id+"F0.wireOp",EDGE,"E15.MirrorCS");var subQ4=sQuery(id+"F0.wireOp",EDGE,"E10");var subQ5=sQuery(id+"F0.wireOp",EDGE,"E9");var subQ6=sQuery(id+"F0.wireOp",EDGE,"E16.MirrorCS");Q14=makeQuery(id+"F8.boolean.opBoolean","INTERSECT",EDGE,{"derivedFrom":[makeQuery(id+"F3.boolean.opBoolean","SPLIT",FACE,{"disambiguationData":[TD([makeQuery(id+"F2.opExtrude","SWEPT_FACE",FACE,{"disambiguationData":[OSD([subQ5])]})])],"derivedFrom":makeQuery(id+"F2.opExtrude","CAP_FACE",FACE,{"disambiguationData":[OSD([subQ5,subQ4,subQ1,sQuery(id+"F0.wireOp",EDGE,"E12"),subQ0,subQ3,subQ6,sQuery(id+"F0.wireOp",EDGE,"E13.MirrorCS"),sQuery(id+"F0.wireOp",EDGE,"E17.MirrorCS"),sQuery(id+"F0.wireOp",EDGE,"E18.MirrorCS"),sQuery(id+"F0.wireOp",EDGE,"E19.MirrorCS"),sQuery(id+"F0.wireOp",EDGE,"E20.MirrorCS"),sQuery(id+"F0.wireOp",EDGE,"E21.MirrorCS"),sQuery(id+"F0.wireOp",EDGE,"E22.MirrorCS"),sQuery(id+"F0.wireOp",EDGE,"E23.MirrorCS"),sQuery(id+"F0.wireOp",EDGE,"E24.MirrorCS")])],"isStart":true})}),makeQuery(id+"F8.opExtrude","SWEPT_FACE",FACE,{"disambiguationData":[OSD([sQuery(id+"F7.wireOp",EDGE,"E34.MirrorC")])]})]});}
            var Q15;
            {var subQ0=sQuery(id+"F0.wireOp",EDGE,"E14.MirrorCS");var subQ1=sQuery(id+"F0.wireOp",EDGE,"E11");var subQ3=sQuery(id+"F0.wireOp",EDGE,"E15.MirrorCS");var subQ4=sQuery(id+"F0.wireOp",EDGE,"E10");var subQ5=sQuery(id+"F0.wireOp",EDGE,"E9");var subQ6=sQuery(id+"F0.wireOp",EDGE,"E16.MirrorCS");Q15=makeQuery(id+"F8.boolean.opBoolean","INTERSECT",EDGE,{"derivedFrom":[makeQuery(id+"F3.boolean.opBoolean","SPLIT",FACE,{"disambiguationData":[TD([makeQuery(id+"F2.opExtrude","SWEPT_FACE",FACE,{"disambiguationData":[OSD([subQ5])]})])],"derivedFrom":makeQuery(id+"F2.opExtrude","CAP_FACE",FACE,{"disambiguationData":[OSD([subQ5,subQ4,subQ1,sQuery(id+"F0.wireOp",EDGE,"E12"),subQ0,subQ3,subQ6,sQuery(id+"F0.wireOp",EDGE,"E13.MirrorCS"),sQuery(id+"F0.wireOp",EDGE,"E17.MirrorCS"),sQuery(id+"F0.wireOp",EDGE,"E18.MirrorCS"),sQuery(id+"F0.wireOp",EDGE,"E19.MirrorCS"),sQuery(id+"F0.wireOp",EDGE,"E20.MirrorCS"),sQuery(id+"F0.wireOp",EDGE,"E21.MirrorCS"),sQuery(id+"F0.wireOp",EDGE,"E22.MirrorCS"),sQuery(id+"F0.wireOp",EDGE,"E23.MirrorCS"),sQuery(id+"F0.wireOp",EDGE,"E24.MirrorCS")])],"isStart":true})}),makeQuery(id+"F8.opExtrude","SWEPT_FACE",FACE,{"disambiguationData":[OSD([sQuery(id+"F7.wireOp",EDGE,"E31")])]})]});}
            var Q16;
            {var subQ0=sQuery(id+"F0.wireOp",EDGE,"E14.MirrorCS");var subQ1=sQuery(id+"F0.wireOp",EDGE,"E11");var subQ3=sQuery(id+"F0.wireOp",EDGE,"E15.MirrorCS");var subQ4=sQuery(id+"F0.wireOp",EDGE,"E10");var subQ5=sQuery(id+"F0.wireOp",EDGE,"E9");var subQ6=sQuery(id+"F0.wireOp",EDGE,"E16.MirrorCS");Q16=makeQuery(id+"F8.boolean.opBoolean","INTERSECT",EDGE,{"derivedFrom":[makeQuery(id+"F3.boolean.opBoolean","SPLIT",FACE,{"disambiguationData":[TD([makeQuery(id+"F2.opExtrude","SWEPT_FACE",FACE,{"disambiguationData":[OSD([subQ5])]})])],"derivedFrom":makeQuery(id+"F2.opExtrude","CAP_FACE",FACE,{"disambiguationData":[OSD([subQ5,subQ4,subQ1,sQuery(id+"F0.wireOp",EDGE,"E12"),subQ0,subQ3,subQ6,sQuery(id+"F0.wireOp",EDGE,"E13.MirrorCS"),sQuery(id+"F0.wireOp",EDGE,"E17.MirrorCS"),sQuery(id+"F0.wireOp",EDGE,"E18.MirrorCS"),sQuery(id+"F0.wireOp",EDGE,"E19.MirrorCS"),sQuery(id+"F0.wireOp",EDGE,"E20.MirrorCS"),sQuery(id+"F0.wireOp",EDGE,"E21.MirrorCS"),sQuery(id+"F0.wireOp",EDGE,"E22.MirrorCS"),sQuery(id+"F0.wireOp",EDGE,"E23.MirrorCS"),sQuery(id+"F0.wireOp",EDGE,"E24.MirrorCS")])],"isStart":true})}),makeQuery(id+"F8.opExtrude","SWEPT_FACE",FACE,{"disambiguationData":[OSD([sQuery(id+"F7.wireOp",EDGE,"E28")])]})]});}
            var Q17;
            {var subQ0=sQuery(id+"F0.wireOp",EDGE,"E14.MirrorCS");var subQ1=sQuery(id+"F0.wireOp",EDGE,"E11");var subQ3=sQuery(id+"F0.wireOp",EDGE,"E15.MirrorCS");var subQ4=sQuery(id+"F0.wireOp",EDGE,"E10");var subQ5=sQuery(id+"F0.wireOp",EDGE,"E9");var subQ6=sQuery(id+"F0.wireOp",EDGE,"E16.MirrorCS");Q17=makeQuery(id+"F8.boolean.opBoolean","INTERSECT",EDGE,{"derivedFrom":[makeQuery(id+"F3.boolean.opBoolean","SPLIT",FACE,{"disambiguationData":[TD([makeQuery(id+"F2.opExtrude","SWEPT_FACE",FACE,{"disambiguationData":[OSD([subQ5])]})])],"derivedFrom":makeQuery(id+"F2.opExtrude","CAP_FACE",FACE,{"disambiguationData":[OSD([subQ5,subQ4,subQ1,sQuery(id+"F0.wireOp",EDGE,"E12"),subQ0,subQ3,subQ6,sQuery(id+"F0.wireOp",EDGE,"E13.MirrorCS"),sQuery(id+"F0.wireOp",EDGE,"E17.MirrorCS"),sQuery(id+"F0.wireOp",EDGE,"E18.MirrorCS"),sQuery(id+"F0.wireOp",EDGE,"E19.MirrorCS"),sQuery(id+"F0.wireOp",EDGE,"E20.MirrorCS"),sQuery(id+"F0.wireOp",EDGE,"E21.MirrorCS"),sQuery(id+"F0.wireOp",EDGE,"E22.MirrorCS"),sQuery(id+"F0.wireOp",EDGE,"E23.MirrorCS"),sQuery(id+"F0.wireOp",EDGE,"E24.MirrorCS")])],"isStart":true})}),makeQuery(id+"F8.opExtrude","SWEPT_FACE",FACE,{"disambiguationData":[OSD([sQuery(id+"F7.wireOp",EDGE,"E27")])]})]});}
            var Q18;
            {var subQ0=sQuery(id+"F0.wireOp",EDGE,"E22.MirrorCS");var subQ1=sQuery(id+"F0.wireOp",EDGE,"E20.MirrorCS");var subQ2=sQuery(id+"F0.wireOp",EDGE,"E18.MirrorCS");var subQ3=sQuery(id+"F0.wireOp",EDGE,"E24.MirrorCS");var subQ4=sQuery(id+"F0.wireOp",EDGE,"E17.MirrorCS");var subQ5=sQuery(id+"F0.wireOp",EDGE,"E23.MirrorCS");Q18=makeQuery(id+"F8.boolean.opBoolean","INTERSECT",EDGE,{"derivedFrom":[makeQuery(id+"F3.boolean.opBoolean","SPLIT",FACE,{"disambiguationData":[TD([makeQuery(id+"F2.opExtrude","SWEPT_FACE",FACE,{"disambiguationData":[OSD([subQ2])]})])],"derivedFrom":makeQuery(id+"F2.opExtrude","CAP_FACE",FACE,{"disambiguationData":[OSD([sQuery(id+"F0.wireOp",EDGE,"E9"),sQuery(id+"F0.wireOp",EDGE,"E10"),sQuery(id+"F0.wireOp",EDGE,"E11"),sQuery(id+"F0.wireOp",EDGE,"E12"),sQuery(id+"F0.wireOp",EDGE,"E14.MirrorCS"),sQuery(id+"F0.wireOp",EDGE,"E15.MirrorCS"),sQuery(id+"F0.wireOp",EDGE,"E16.MirrorCS"),sQuery(id+"F0.wireOp",EDGE,"E13.MirrorCS"),subQ4,subQ2,sQuery(id+"F0.wireOp",EDGE,"E19.MirrorCS"),subQ1,sQuery(id+"F0.wireOp",EDGE,"E21.MirrorCS"),subQ0,subQ5,subQ3])],"isStart":true})}),makeQuery(id+"F8.opExtrude","SWEPT_FACE",FACE,{"disambiguationData":[OSD([sQuery(id+"F7.wireOp",EDGE,"E40.MirrorC")])]})]});}
            var Q19;
            {var subQ0=sQuery(id+"F0.wireOp",EDGE,"E22.MirrorCS");var subQ1=sQuery(id+"F0.wireOp",EDGE,"E20.MirrorCS");var subQ2=sQuery(id+"F0.wireOp",EDGE,"E18.MirrorCS");var subQ3=sQuery(id+"F0.wireOp",EDGE,"E24.MirrorCS");var subQ4=sQuery(id+"F0.wireOp",EDGE,"E17.MirrorCS");var subQ5=sQuery(id+"F0.wireOp",EDGE,"E23.MirrorCS");Q19=makeQuery(id+"F8.boolean.opBoolean","INTERSECT",EDGE,{"derivedFrom":[makeQuery(id+"F3.boolean.opBoolean","SPLIT",FACE,{"disambiguationData":[TD([makeQuery(id+"F2.opExtrude","SWEPT_FACE",FACE,{"disambiguationData":[OSD([subQ2])]})])],"derivedFrom":makeQuery(id+"F2.opExtrude","CAP_FACE",FACE,{"disambiguationData":[OSD([sQuery(id+"F0.wireOp",EDGE,"E9"),sQuery(id+"F0.wireOp",EDGE,"E10"),sQuery(id+"F0.wireOp",EDGE,"E11"),sQuery(id+"F0.wireOp",EDGE,"E12"),sQuery(id+"F0.wireOp",EDGE,"E14.MirrorCS"),sQuery(id+"F0.wireOp",EDGE,"E15.MirrorCS"),sQuery(id+"F0.wireOp",EDGE,"E16.MirrorCS"),sQuery(id+"F0.wireOp",EDGE,"E13.MirrorCS"),subQ4,subQ2,sQuery(id+"F0.wireOp",EDGE,"E19.MirrorCS"),subQ1,sQuery(id+"F0.wireOp",EDGE,"E21.MirrorCS"),subQ0,subQ5,subQ3])],"isStart":true})}),makeQuery(id+"F8.opExtrude","SWEPT_FACE",FACE,{"disambiguationData":[OSD([sQuery(id+"F7.wireOp",EDGE,"E39.MirrorC")])]})]});}
            var Q20;
            {var subQ0=sQuery(id+"F0.wireOp",EDGE,"E22.MirrorCS");var subQ1=sQuery(id+"F0.wireOp",EDGE,"E20.MirrorCS");var subQ2=sQuery(id+"F0.wireOp",EDGE,"E18.MirrorCS");var subQ3=sQuery(id+"F0.wireOp",EDGE,"E24.MirrorCS");var subQ4=sQuery(id+"F0.wireOp",EDGE,"E17.MirrorCS");var subQ5=sQuery(id+"F0.wireOp",EDGE,"E23.MirrorCS");Q20=makeQuery(id+"F8.boolean.opBoolean","INTERSECT",EDGE,{"derivedFrom":[makeQuery(id+"F3.boolean.opBoolean","SPLIT",FACE,{"disambiguationData":[TD([makeQuery(id+"F2.opExtrude","SWEPT_FACE",FACE,{"disambiguationData":[OSD([subQ2])]})])],"derivedFrom":makeQuery(id+"F2.opExtrude","CAP_FACE",FACE,{"disambiguationData":[OSD([sQuery(id+"F0.wireOp",EDGE,"E9"),sQuery(id+"F0.wireOp",EDGE,"E10"),sQuery(id+"F0.wireOp",EDGE,"E11"),sQuery(id+"F0.wireOp",EDGE,"E12"),sQuery(id+"F0.wireOp",EDGE,"E14.MirrorCS"),sQuery(id+"F0.wireOp",EDGE,"E15.MirrorCS"),sQuery(id+"F0.wireOp",EDGE,"E16.MirrorCS"),sQuery(id+"F0.wireOp",EDGE,"E13.MirrorCS"),subQ4,subQ2,sQuery(id+"F0.wireOp",EDGE,"E19.MirrorCS"),subQ1,sQuery(id+"F0.wireOp",EDGE,"E21.MirrorCS"),subQ0,subQ5,subQ3])],"isStart":true})}),makeQuery(id+"F8.opExtrude","SWEPT_FACE",FACE,{"disambiguationData":[OSD([sQuery(id+"F7.wireOp",EDGE,"E38.MirrorC")])]})]});}
            var Q21;
            {var subQ0=sQuery(id+"F0.wireOp",EDGE,"E22.MirrorCS");var subQ1=sQuery(id+"F0.wireOp",EDGE,"E20.MirrorCS");var subQ2=sQuery(id+"F0.wireOp",EDGE,"E18.MirrorCS");var subQ3=sQuery(id+"F0.wireOp",EDGE,"E24.MirrorCS");var subQ4=sQuery(id+"F0.wireOp",EDGE,"E17.MirrorCS");var subQ5=sQuery(id+"F0.wireOp",EDGE,"E23.MirrorCS");Q21=makeQuery(id+"F8.boolean.opBoolean","INTERSECT",EDGE,{"derivedFrom":[makeQuery(id+"F3.boolean.opBoolean","SPLIT",FACE,{"disambiguationData":[TD([makeQuery(id+"F2.opExtrude","SWEPT_FACE",FACE,{"disambiguationData":[OSD([subQ2])]})])],"derivedFrom":makeQuery(id+"F2.opExtrude","CAP_FACE",FACE,{"disambiguationData":[OSD([sQuery(id+"F0.wireOp",EDGE,"E9"),sQuery(id+"F0.wireOp",EDGE,"E10"),sQuery(id+"F0.wireOp",EDGE,"E11"),sQuery(id+"F0.wireOp",EDGE,"E12"),sQuery(id+"F0.wireOp",EDGE,"E14.MirrorCS"),sQuery(id+"F0.wireOp",EDGE,"E15.MirrorCS"),sQuery(id+"F0.wireOp",EDGE,"E16.MirrorCS"),sQuery(id+"F0.wireOp",EDGE,"E13.MirrorCS"),subQ4,subQ2,sQuery(id+"F0.wireOp",EDGE,"E19.MirrorCS"),subQ1,sQuery(id+"F0.wireOp",EDGE,"E21.MirrorCS"),subQ0,subQ5,subQ3])],"isStart":true})}),makeQuery(id+"F8.opExtrude","SWEPT_FACE",FACE,{"disambiguationData":[OSD([sQuery(id+"F7.wireOp",EDGE,"E37.MirrorC")])]})]});}
            var Q22;
            {var subQ0=sQuery(id+"F0.wireOp",EDGE,"E22.MirrorCS");var subQ1=sQuery(id+"F0.wireOp",EDGE,"E20.MirrorCS");var subQ2=sQuery(id+"F0.wireOp",EDGE,"E18.MirrorCS");var subQ3=sQuery(id+"F0.wireOp",EDGE,"E24.MirrorCS");var subQ4=sQuery(id+"F0.wireOp",EDGE,"E17.MirrorCS");var subQ5=sQuery(id+"F0.wireOp",EDGE,"E23.MirrorCS");Q22=makeQuery(id+"F8.boolean.opBoolean","INTERSECT",EDGE,{"derivedFrom":[makeQuery(id+"F3.boolean.opBoolean","SPLIT",FACE,{"disambiguationData":[TD([makeQuery(id+"F2.opExtrude","SWEPT_FACE",FACE,{"disambiguationData":[OSD([subQ2])]})])],"derivedFrom":makeQuery(id+"F2.opExtrude","CAP_FACE",FACE,{"disambiguationData":[OSD([sQuery(id+"F0.wireOp",EDGE,"E9"),sQuery(id+"F0.wireOp",EDGE,"E10"),sQuery(id+"F0.wireOp",EDGE,"E11"),sQuery(id+"F0.wireOp",EDGE,"E12"),sQuery(id+"F0.wireOp",EDGE,"E14.MirrorCS"),sQuery(id+"F0.wireOp",EDGE,"E15.MirrorCS"),sQuery(id+"F0.wireOp",EDGE,"E16.MirrorCS"),sQuery(id+"F0.wireOp",EDGE,"E13.MirrorCS"),subQ4,subQ2,sQuery(id+"F0.wireOp",EDGE,"E19.MirrorCS"),subQ1,sQuery(id+"F0.wireOp",EDGE,"E21.MirrorCS"),subQ0,subQ5,subQ3])],"isStart":true})}),makeQuery(id+"F8.opExtrude","SWEPT_FACE",FACE,{"disambiguationData":[OSD([sQuery(id+"F7.wireOp",EDGE,"E36.MirrorC")])]})]});}
            var Q23;
            {var subQ0=sQuery(id+"F0.wireOp",EDGE,"E22.MirrorCS");var subQ1=sQuery(id+"F0.wireOp",EDGE,"E20.MirrorCS");var subQ2=sQuery(id+"F0.wireOp",EDGE,"E18.MirrorCS");var subQ3=sQuery(id+"F0.wireOp",EDGE,"E24.MirrorCS");var subQ4=sQuery(id+"F0.wireOp",EDGE,"E17.MirrorCS");var subQ5=sQuery(id+"F0.wireOp",EDGE,"E23.MirrorCS");Q23=makeQuery(id+"F8.boolean.opBoolean","INTERSECT",EDGE,{"derivedFrom":[makeQuery(id+"F3.boolean.opBoolean","SPLIT",FACE,{"disambiguationData":[TD([makeQuery(id+"F2.opExtrude","SWEPT_FACE",FACE,{"disambiguationData":[OSD([subQ2])]})])],"derivedFrom":makeQuery(id+"F2.opExtrude","CAP_FACE",FACE,{"disambiguationData":[OSD([sQuery(id+"F0.wireOp",EDGE,"E9"),sQuery(id+"F0.wireOp",EDGE,"E10"),sQuery(id+"F0.wireOp",EDGE,"E11"),sQuery(id+"F0.wireOp",EDGE,"E12"),sQuery(id+"F0.wireOp",EDGE,"E14.MirrorCS"),sQuery(id+"F0.wireOp",EDGE,"E15.MirrorCS"),sQuery(id+"F0.wireOp",EDGE,"E16.MirrorCS"),sQuery(id+"F0.wireOp",EDGE,"E13.MirrorCS"),subQ4,subQ2,sQuery(id+"F0.wireOp",EDGE,"E19.MirrorCS"),subQ1,sQuery(id+"F0.wireOp",EDGE,"E21.MirrorCS"),subQ0,subQ5,subQ3])],"isStart":true})}),makeQuery(id+"F8.opExtrude","SWEPT_FACE",FACE,{"disambiguationData":[OSD([sQuery(id+"F7.wireOp",EDGE,"E35.MirrorC")])]})]});}
            fillet(context, id + "F9", {"entities" : qUnion([Q0, Q1, Q2, Q3, Q4, Q5, Q6, Q7, Q8, Q9, Q10, Q11, Q12, Q13, Q14, Q15, Q16, Q17, Q18, Q19, Q20, Q21, Q22, Q23]), "radius" : 1.52 * mm, "tangentPropagation" : true, "allowEdgeOverflow" : false});
        }
        {
            var Q0;
            Q0=qCreatedBy(makeId("Front.planeOp"),FACE);
            var sketch = newSketch(context, id + "F10", { "sketchPlane" : qUnion([Q0])});
            skCircle(sketch, "E41", {"center": v(0, 0) * mm, "radius": 28.58 * mm});
            skSolve(sketch);
        }
        {
            var Q0;
            Q0 = qSketchRegion(id + "F10", true);
            extrude(context, id + "F11", {"entities" : qUnion([Q0]), "operationType" : NewBodyOperationType.ADD, "depth" : 10.16 * mm, "hasSecondDirection" : true, "secondDirectionOppositeDirection" : true, "secondDirectionDepth" : 10.16 * mm});
        }
    });
